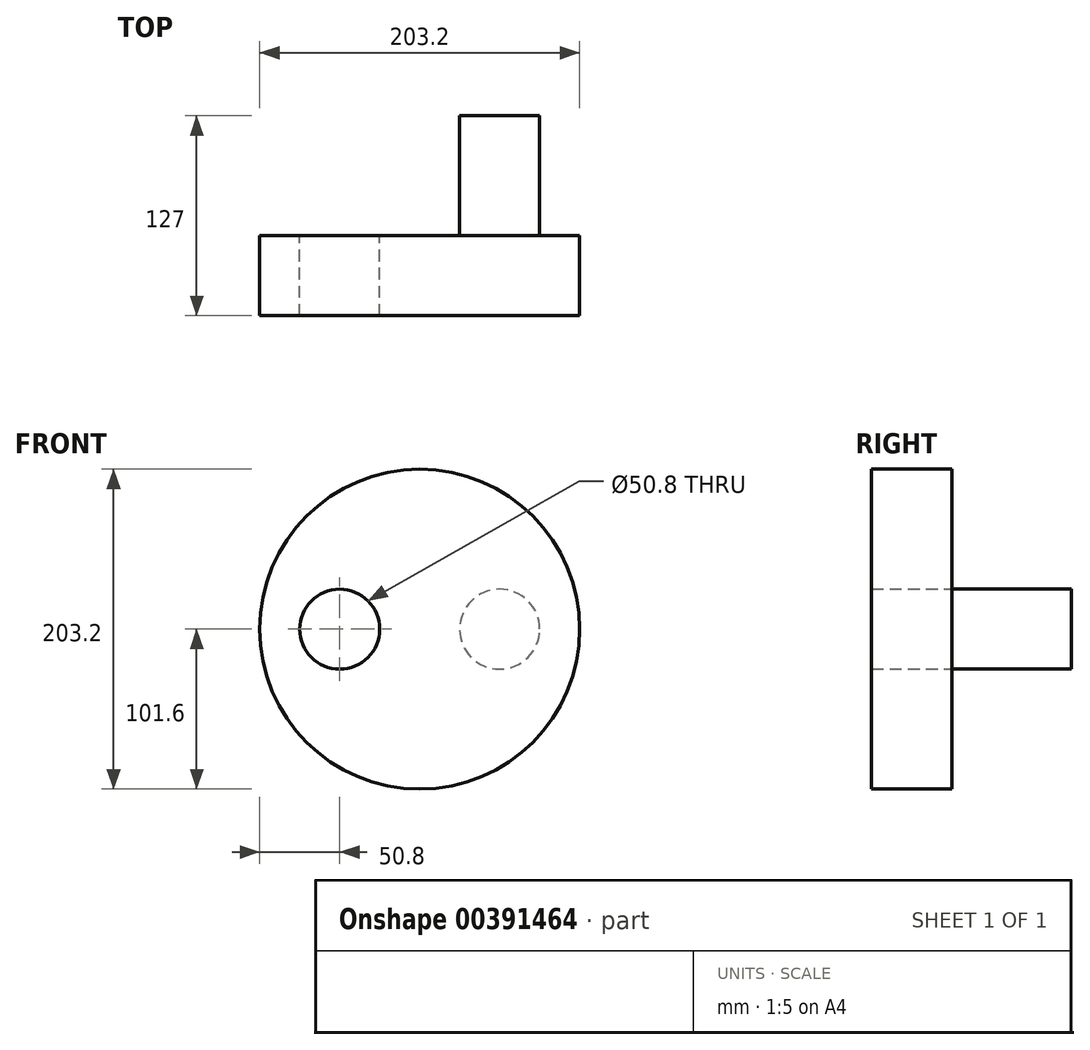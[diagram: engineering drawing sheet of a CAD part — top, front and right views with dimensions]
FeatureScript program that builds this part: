
annotation { "Feature Type Name" : "Feature", "Feature Type Description" : "" }
export const myFeature = defineFeature(function(context is Context, id is Id, definition is map)
    precondition{}
    {
        {
            var Q0;
            Q0=qCreatedBy(makeId("Front.planeOp"),FACE);
            var sketch = newSketch(context, id + "F0", { "sketchPlane" : qUnion([Q0])});
            skCircle(sketch, "E0", {"center": v(0, 0) * mm, "radius": 101.6 * mm});
            skCircle(sketch, "E1", {"center": v(-50.8, 0) * mm, "radius": 25.4 * mm});
            skCircle(sketch, "E2", {"center": v(50.8, 0) * mm, "radius": 25.4 * mm});
            skSolve(sketch);
        }
        {
            var Q0;
            Q0 = qSketchRegion(id + "F0", true);
            var Q1;
            Q1=makeQuery(id+"F0.imprint","IMPRINT",FACE,{"disambiguationData":[TD([[makeQuery(id+"F0.imprint","IMPRINT",EDGE,{"derivedFrom":sQuery(id+"F0.wireOp",EDGE,"E2")}),1.0]])]});
            extrude(context, id + "F1", {"entities" : qUnion([Q0, Q1]), "depth" : 50.8 * mm});
        }
        {
            var Q0;
            Q0=makeQuery(id+"F0.imprint","IMPRINT",FACE,{"disambiguationData":[TD([[makeQuery(id+"F0.imprint","IMPRINT",EDGE,{"derivedFrom":sQuery(id+"F0.wireOp",EDGE,"E2")}),1.0]])]});
            extrude(context, id + "F2", {"entities" : qUnion([Q0]), "operationType" : NewBodyOperationType.ADD, "oppositeDirection" : true, "depth" : 76.2 * mm});
        }
    });
